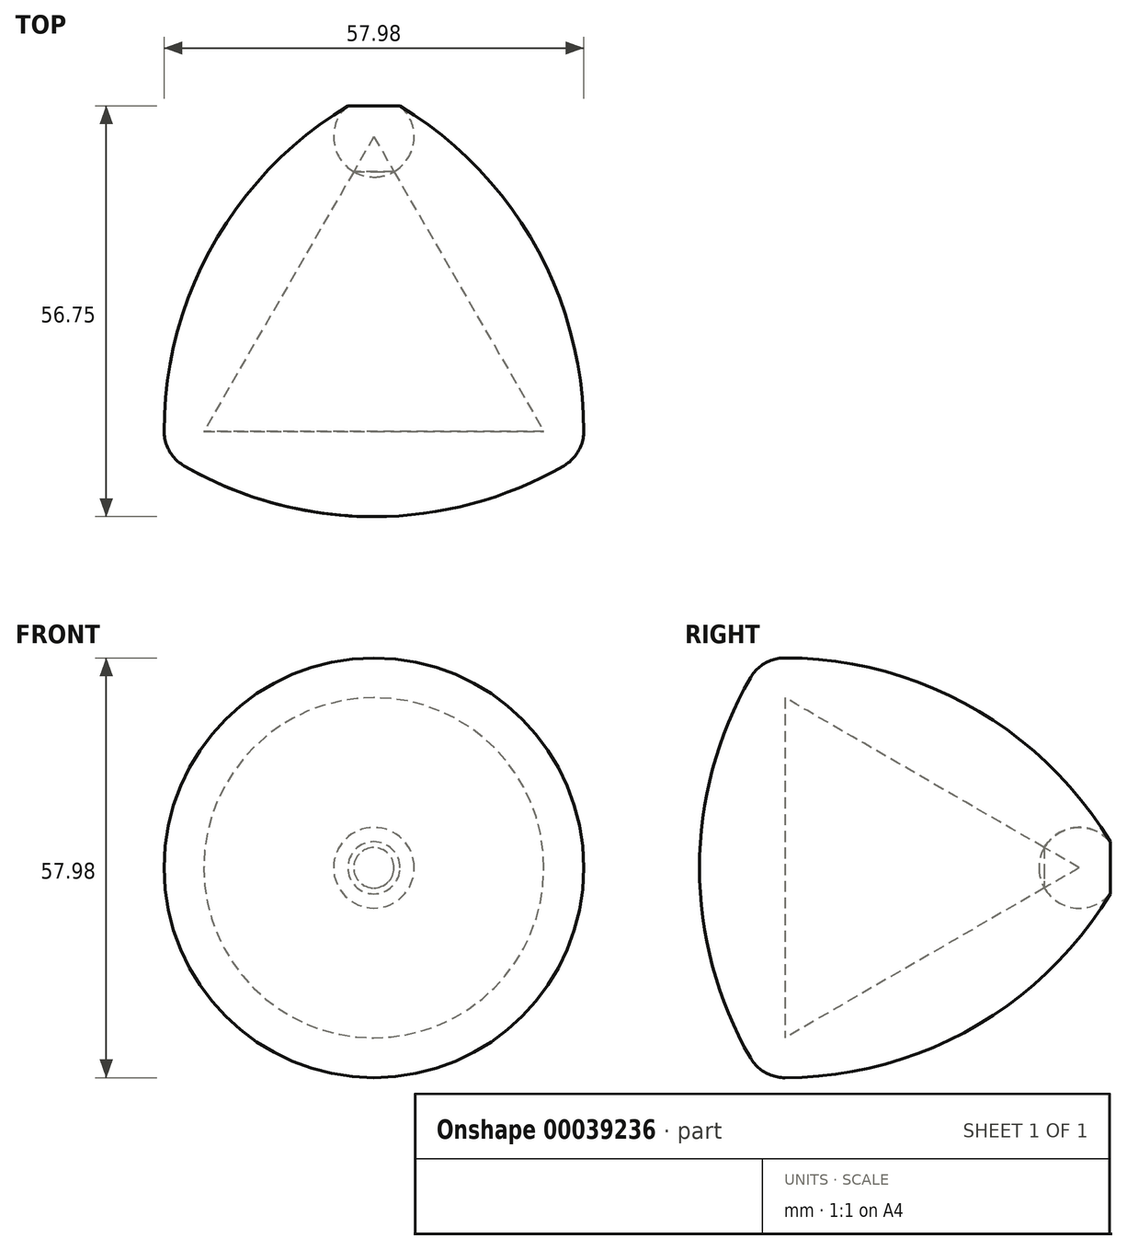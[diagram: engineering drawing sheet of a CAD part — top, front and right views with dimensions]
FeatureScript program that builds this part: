
annotation { "Feature Type Name" : "Feature", "Feature Type Description" : "" }
export const myFeature = defineFeature(function(context is Context, id is Id, definition is map)
    precondition{}
    {
        {
            var Q0;
            Q0=qCreatedBy(makeId("Top.planeOp"),FACE);
            var sketch = newSketch(context, id + "F0", { "sketchPlane" : qUnion([Q0])});
            skLineSegment(sketch, "E0", {"start": v(0, 27.5) * mm, "end": v(-23.5, -13.18) * mm});
            skLineSegment(sketch, "E1", {"start": v(-23.5, -13.18) * mm, "end": v(23.5, -13.18) * mm});
            skLineSegment(sketch, "E2", {"start": v(23.5, -13.18) * mm, "end": v(0, 27.5) * mm});
            skCircle(sketch, "E3", {"center": v(-23.5, -13.18) * mm, "radius": 5.5 * mm});
            skCircle(sketch, "E4", {"center": v(0, 27.5) * mm, "radius": 5.58 * mm});
            skCircle(sketch, "E5", {"center": v(23.5, -13.18) * mm, "radius": 5.5 * mm});
            skCircle(sketch, "E6", {"center": v(0, 27.5) * mm, "radius": 52.48 * mm});
            skCircle(sketch, "E7", {"center": v(-23.5, -13.18) * mm, "radius": 52.48 * mm});
            skCircle(sketch, "E8", {"center": v(23.5, -13.18) * mm, "radius": 52.48 * mm});
            skLineSegment(sketch, "E9", {"start": v(0, 33.75) * mm, "end": v(0, -24.98) * mm});
            skSolve(sketch);
        }
        {
            var Q0;
            {var subQ3=sQuery(id+"F0.wireOp",EDGE,"E0");var subQ5=sQuery(id+"F0.wireOp",EDGE,"E4");var subQ7=makeQuery(id+"F0.imprint","INTERSECT",VERTEX,{"derivedFrom":[subQ3,subQ5]});Q0=makeQuery(id+"F0.imprint","IMPRINT",FACE,{"disambiguationData":[TD([[makeQuery(id+"F0.imprint","IMPRINT",EDGE,{"disambiguationData":[TD([[subQ7,-1.0]])],"derivedFrom":subQ3}),-1.0]])]});}
            var Q1;
            {var subQ2=sQuery(id+"F0.wireOp",EDGE,"E1");var subQ4=sQuery(id+"F0.wireOp",EDGE,"E0");var subQ6=makeQuery(id+"F0.imprint","INTERSECT",VERTEX,{"derivedFrom":[subQ4,subQ2]});Q1=makeQuery(id+"F0.imprint","IMPRINT",FACE,{"disambiguationData":[TD([[makeQuery(id+"F0.imprint","IMPRINT",EDGE,{"disambiguationData":[TD([[subQ6,1.0]])],"derivedFrom":subQ4}),-1.0]])]});}
            var Q2;
            {var subQ3=sQuery(id+"F0.wireOp",EDGE,"E3");var subQ5=sQuery(id+"F0.wireOp",EDGE,"E1");var subQ6=makeQuery(id+"F0.imprint","INTERSECT",VERTEX,{"derivedFrom":[subQ5,subQ3]});Q2=makeQuery(id+"F0.imprint","IMPRINT",FACE,{"disambiguationData":[TD([[makeQuery(id+"F0.imprint","IMPRINT",EDGE,{"disambiguationData":[TD([[subQ6,-1.0]])],"derivedFrom":subQ5}),-1.0]])]});}
            var Q3;
            {var subQ0=sQuery(id+"F0.wireOp",EDGE,"E9");var subQ1=sQuery(id+"F0.wireOp",EDGE,"E4");var subQ2=makeQuery(id+"F0.imprint","INTERSECT",VERTEX,{"disambiguationData":[OD(0.0)],"derivedFrom":[subQ1,subQ0]});Q3=makeQuery(id+"F0.imprint","IMPRINT",FACE,{"disambiguationData":[TD([[makeQuery(id+"F0.imprint","IMPRINT",EDGE,{"disambiguationData":[TD([[subQ2,-1.0]])],"derivedFrom":subQ1}),1.0]])]});}
            var Q4;
            Q4=sQuery(id+"F0.wireOp",EDGE,"E9");
            revolve(context, id + "F1", {"entities" : qUnion([Q0, Q1, Q2, Q3]), "axis" : qUnion([Q4]), "revolveType" : RevolveType.FULL});
        }
    });
